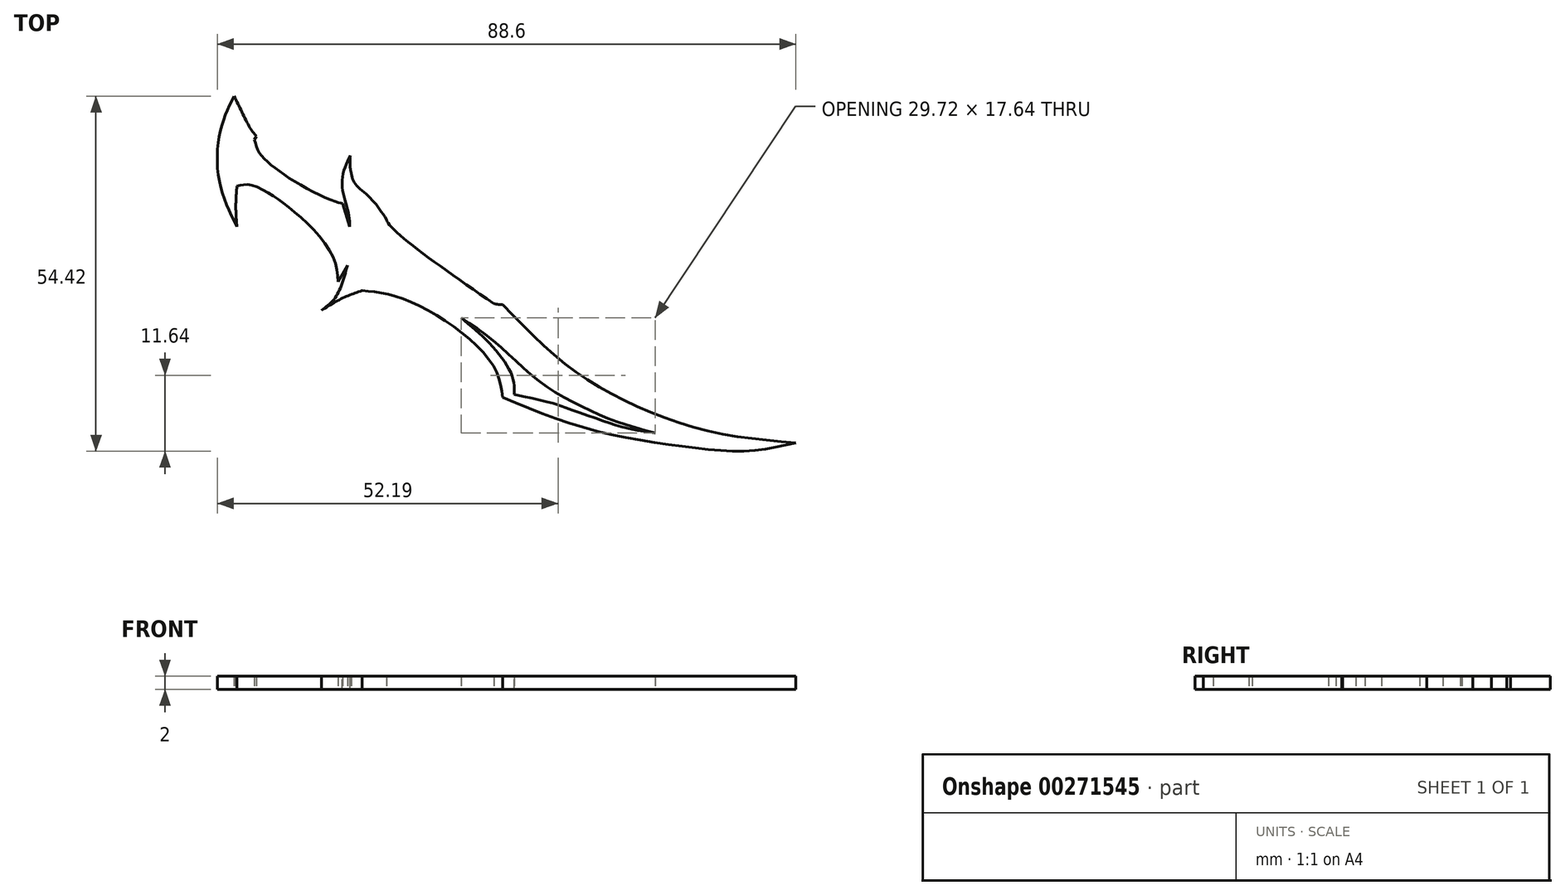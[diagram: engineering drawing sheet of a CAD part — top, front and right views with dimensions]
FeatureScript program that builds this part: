
annotation { "Feature Type Name" : "Feature", "Feature Type Description" : "" }
export const myFeature = defineFeature(function(context is Context, id is Id, definition is map)
    precondition{}
    {
        {
            var Q0;
            Q0=qCreatedBy(makeId("Top.planeOp"),FACE);
            var sketch = newSketch(context, id + "F0", { "sketchPlane" : qUnion([Q0])});
            skFitSpline(sketch, "E0", {"points": [v(-36.9, 31.67) * mm, v(-39, 26.43) * mm, v(-39.16, 18.64) * mm, v(-36.47, 11.64) * mm], "startDerivative": vector(-8.07, -16.2) * mm, "endDerivative": vector(9.48, -19.38) * mm});
            skFitSpline(sketch, "E1", {"points": [v(-36.9, 31.67) * mm, v(-35.62, 29.05) * mm, v(-34.3, 26.56) * mm, v(-33.48, 25.54) * mm], "startDerivative": vector(3.32, -6.8) * mm, "endDerivative": vector(3.18, -3.45) * mm});
            skFitSpline(sketch, "E2", {"points": [v(-36.47, 11.64) * mm, v(-36.64, 14.75) * mm, v(-36.47, 17.86) * mm], "startDerivative": vector(-0.52, 6.22) * mm, "endDerivative": vector(0.52, 6.21) * mm});
            skFitSpline(sketch, "E3", {"points": [v(-36.47, 17.86) * mm, v(-35.54, 18.08) * mm, v(-34.09, 18) * mm, v(-31.41, 16.67) * mm, v(-28.79, 14.82) * mm, v(-24.48, 10.98) * mm, v(-21.47, 6.34) * mm, v(-20.98, 3.25) * mm], "startDerivative": vector(11.15, 3.12) * mm, "endDerivative": vector(1.04, -20.53) * mm});
            skFitSpline(sketch, "E4", {"points": [v(-33.48, 25.54) * mm, v(-33.79, 25) * mm], "startDerivative": vector(-0.3, -0.54) * mm, "endDerivative": vector(-0.3, -0.54) * mm});
            skFitSpline(sketch, "E5", {"points": [v(-33.79, 25) * mm, v(-33.13, 23.16) * mm, v(-31.3, 21.21) * mm, v(-26.64, 18.02) * mm, v(-21.18, 15.42) * mm, v(-20.26, 15.24) * mm], "startDerivative": vector(3.11, -11.94) * mm, "endDerivative": vector(6.6, -0.53) * mm});
            skFitSpline(sketch, "E6", {"points": [v(-20.26, 15.24) * mm, v(-19.17, 11.64) * mm], "startDerivative": vector(1.08, -3.6) * mm, "endDerivative": vector(1.08, -3.6) * mm});
            skFitSpline(sketch, "E7", {"points": [v(-20.98, 3.25) * mm, v(-19.54, 5.79) * mm], "startDerivative": vector(1.45, 2.53) * mm, "endDerivative": vector(1.45, 2.53) * mm});
            skFitSpline(sketch, "E8", {"points": [v(-19.54, 5.79) * mm, v(-20.58, 2.37) * mm, v(-21.89, 0.22) * mm, v(-23.55, -1.16) * mm], "startDerivative": vector(-2.46, -9.44) * mm, "endDerivative": vector(-5.9, -4.27) * mm});
            skFitSpline(sketch, "E9", {"points": [v(-17.32, 1.86) * mm, v(-20.25, 0.74) * mm, v(-23.55, -1.16) * mm], "startDerivative": vector(-6.12, -2.07) * mm, "endDerivative": vector(-6.34, -3.95) * mm});
            skFitSpline(sketch, "E10", {"points": [v(-19.17, 11.64) * mm, v(-19.42, 13.93) * mm, v(-20.17, 16.68) * mm, v(-20.2, 19.83) * mm, v(-19.1, 22.62) * mm], "startDerivative": vector(-0.46, 10) * mm, "endDerivative": vector(5.11, 10.47) * mm});
            skFitSpline(sketch, "E11", {"points": [v(-19.1, 22.62) * mm, v(-18.92, 19.79) * mm, v(-17.48, 17.44) * mm, v(-16.95, 17.06) * mm, v(-15.55, 15.93) * mm, v(-13.75, 13.55) * mm, v(-13.32, 12.24) * mm, v(2.88, -0.13) * mm], "startDerivative": vector(-1.66, -21.39) * mm, "endDerivative": vector(63.97, -44.33) * mm});
            skFitSpline(sketch, "E12", {"points": [v(2.88, -0.13) * mm, v(3.6, -0.25) * mm, v(4.22, -0.25) * mm], "startDerivative": vector(1.41, -0.3) * mm, "endDerivative": vector(1.27, 0.06) * mm});
            skFitSpline(sketch, "E13", {"points": [v(-17.32, 1.86) * mm, v(-12.38, 1.05) * mm, v(-3.82, -3.23) * mm, v(2.97, -9.96) * mm, v(4.22, -14.48) * mm], "startDerivative": vector(21.98, -1.87) * mm, "endDerivative": vector(2.75, -21.58) * mm});
            skFitSpline(sketch, "E14", {"points": [v(4.22, -14.48) * mm, v(17.35, -19.33) * mm, v(31.43, -21.95) * mm, v(41.75, -22.71) * mm, v(49.12, -21.46) * mm], "startDerivative": vector(46.13, -19.37) * mm, "endDerivative": vector(35.08, 8.25) * mm});
            skFitSpline(sketch, "E15", {"points": [v(4.22, -0.25) * mm, v(13.27, -8.95) * mm, v(23.22, -15.12) * mm, v(36.03, -19.73) * mm, v(49.12, -21.46) * mm], "startDerivative": vector(35.62, -37.25) * mm, "endDerivative": vector(51.46, -4.27) * mm});
            skFitSpline(sketch, "E16", {"points": [v(-2.15, -2.29) * mm, v(2.74, -6.77) * mm, v(5.75, -11.4) * mm, v(5.98, -14.02) * mm], "startDerivative": vector(12.94, -10.77) * mm, "endDerivative": vector(-0.5, -10) * mm});
            skFitSpline(sketch, "E17", {"points": [v(5.98, -14.02) * mm, v(12.38, -15.53) * mm, v(13.09, -15.8) * mm, v(19, -17.89) * mm, v(23.57, -19.29) * mm, v(27.57, -19.93) * mm], "startDerivative": vector(32.68, -7.3) * mm, "endDerivative": vector(20.5, -2.67) * mm});
            skFitSpline(sketch, "E18", {"points": [v(-2.15, -2.29) * mm, v(2.56, -5.61) * mm, v(7.06, -9.7) * mm, v(11.74, -13.37) * mm, v(16.98, -16.21) * mm, v(21.98, -18.33) * mm, v(27.57, -19.93) * mm], "startDerivative": vector(28.99, -18.93) * mm, "endDerivative": vector(34.3, -8.9) * mm});
            skFitSpline(sketch, "E19", {"points": [v(-18.92, 19.79) * mm, v(-18.37, 18.24) * mm, v(-16.16, 16.2) * mm, v(-13.56, 12.76) * mm], "startDerivative": vector(1.22, -6.3) * mm, "endDerivative": vector(6.03, -9.13) * mm});
            skSolve(sketch);
        }
        {
            var Q0;
            Q0=makeQuery(id+"F0.imprint","IMPRINT",FACE,{"disambiguationData":[TD([[makeQuery(id+"F0.imprint","IMPRINT",EDGE,{"derivedFrom":sQuery(id+"F0.wireOp",EDGE,"E0")}),1.0]])]});
            extrude(context, id + "F1", {"entities" : qUnion([Q0]), "depth" : 2 * mm, "offsetDistance" : 25 * mm});
        }
    });
